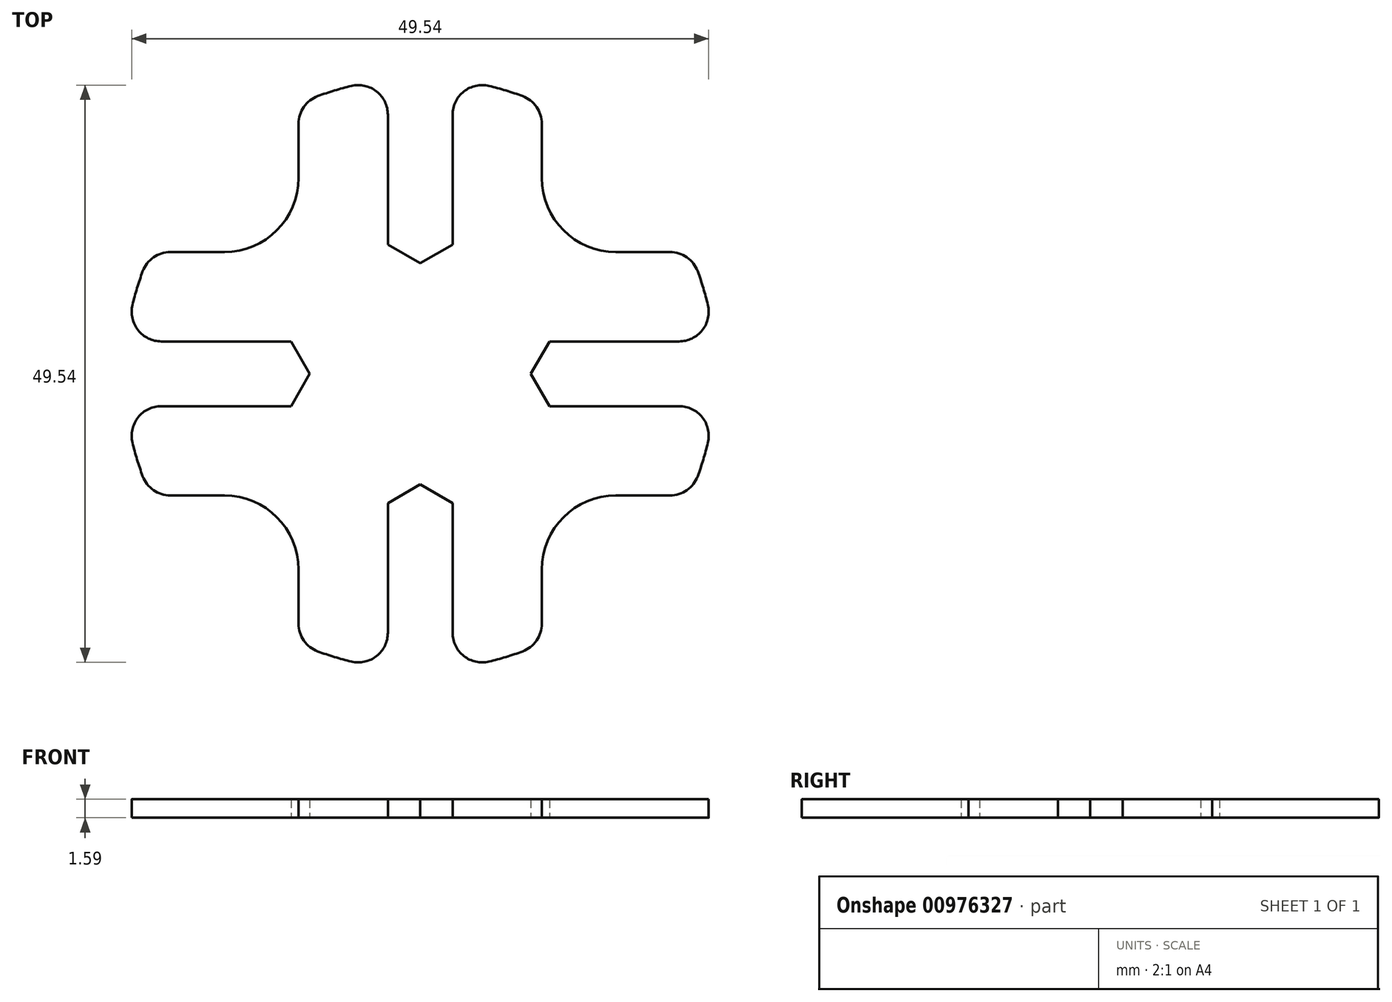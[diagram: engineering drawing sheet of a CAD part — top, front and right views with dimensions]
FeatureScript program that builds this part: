
annotation { "Feature Type Name" : "Feature", "Feature Type Description" : "" }
export const myFeature = defineFeature(function(context is Context, id is Id, definition is map)
    precondition{}
    {
        {
            var Q0;
            Q0=qCreatedBy(makeId("Top.planeOp"),FACE);
            var sketch = newSketch(context, id + "F0", { "sketchPlane" : qUnion([Q0])});
            skCircle(sketch, "E0", {"center": v(0, 0) * mm, "radius": 25.4 * mm});
            skCircle(sketch, "E1.cCircle", {"center": v(0, 12.7) * mm, "radius": 2.78 * mm, "construction": true});
            skLineSegment(sketch, "E1.0", {"start": v(-2.78, 11.1) * mm, "end": v(-2.78, 14.3) * mm});
            skLineSegment(sketch, "E1.1", {"start": v(-2.78, 14.3) * mm, "end": v(0, 15.9) * mm});
            skLineSegment(sketch, "E1.2", {"start": v(0, 15.9) * mm, "end": v(2.78, 14.3) * mm});
            skLineSegment(sketch, "E1.3", {"start": v(2.78, 14.3) * mm, "end": v(2.78, 11.1) * mm});
            skLineSegment(sketch, "E1.4", {"start": v(2.78, 11.1) * mm, "end": v(0, 9.5) * mm});
            skLineSegment(sketch, "E1.5", {"start": v(0, 9.5) * mm, "end": v(-2.78, 11.1) * mm});
            skPoint(sketch, "E1.0.midPoint", {"position": v(-2.78, 12.7) * mm});
            skLineSegment(sketch, "E2", {"start": v(-2.78, 14.3) * mm, "end": v(-2.78, 25.25) * mm});
            skLineSegment(sketch, "E3", {"start": v(2.78, 14.3) * mm, "end": v(2.78, 25.25) * mm});
            skCircle(sketch, "E4.cCircle", {"center": v(0, -12.7) * mm, "radius": 2.78 * mm, "construction": true});
            skLineSegment(sketch, "E4.0", {"start": v(-2.78, -11.1) * mm, "end": v(0, -9.5) * mm});
            skLineSegment(sketch, "E4.1", {"start": v(0, -9.5) * mm, "end": v(2.78, -11.1) * mm});
            skLineSegment(sketch, "E4.2", {"start": v(2.78, -11.1) * mm, "end": v(2.78, -14.3) * mm});
            skLineSegment(sketch, "E4.3", {"start": v(2.78, -14.3) * mm, "end": v(0, -15.9) * mm});
            skLineSegment(sketch, "E4.4", {"start": v(0, -15.9) * mm, "end": v(-2.78, -14.3) * mm});
            skLineSegment(sketch, "E4.5", {"start": v(-2.78, -14.3) * mm, "end": v(-2.78, -11.1) * mm});
            skPoint(sketch, "E4.0.midPoint", {"position": v(-1.39, -10.3) * mm});
            skCircle(sketch, "E5.cCircle", {"center": v(12.7, 0) * mm, "radius": 2.78 * mm, "construction": true});
            skLineSegment(sketch, "E5.0", {"start": v(9.5, 0) * mm, "end": v(11.1, 2.78) * mm});
            skLineSegment(sketch, "E5.1", {"start": v(11.1, 2.78) * mm, "end": v(14.3, 2.78) * mm});
            skLineSegment(sketch, "E5.2", {"start": v(14.3, 2.78) * mm, "end": v(15.9, 0) * mm});
            skLineSegment(sketch, "E5.3", {"start": v(15.9, 0) * mm, "end": v(14.3, -2.78) * mm});
            skLineSegment(sketch, "E5.4", {"start": v(14.3, -2.78) * mm, "end": v(11.1, -2.78) * mm});
            skLineSegment(sketch, "E5.5", {"start": v(11.1, -2.78) * mm, "end": v(9.5, 0) * mm});
            skPoint(sketch, "E5.0.midPoint", {"position": v(10.3, 1.39) * mm});
            skCircle(sketch, "E6.cCircle", {"center": v(-12.7, 0) * mm, "radius": 2.78 * mm, "construction": true});
            skLineSegment(sketch, "E6.0", {"start": v(-15.9, 0) * mm, "end": v(-14.3, 2.78) * mm});
            skLineSegment(sketch, "E6.1", {"start": v(-14.3, 2.78) * mm, "end": v(-11.1, 2.78) * mm});
            skLineSegment(sketch, "E6.2", {"start": v(-11.1, 2.78) * mm, "end": v(-9.5, 0) * mm});
            skLineSegment(sketch, "E6.3", {"start": v(-9.5, 0) * mm, "end": v(-11.1, -2.78) * mm});
            skLineSegment(sketch, "E6.4", {"start": v(-11.1, -2.78) * mm, "end": v(-14.3, -2.78) * mm});
            skLineSegment(sketch, "E6.5", {"start": v(-14.3, -2.78) * mm, "end": v(-15.9, 0) * mm});
            skPoint(sketch, "E6.0.midPoint", {"position": v(-15.1, 1.39) * mm});
            skLineSegment(sketch, "E7", {"start": v(-14.3, -2.78) * mm, "end": v(-25.25, -2.78) * mm});
            skLineSegment(sketch, "E8", {"start": v(-14.3, 2.78) * mm, "end": v(-25.25, 2.78) * mm});
            skLineSegment(sketch, "E9", {"start": v(14.3, 2.78) * mm, "end": v(25.25, 2.78) * mm});
            skLineSegment(sketch, "E10", {"start": v(14.3, -2.78) * mm, "end": v(25.25, -2.78) * mm});
            skLineSegment(sketch, "E11", {"start": v(2.78, -14.3) * mm, "end": v(2.78, -25.25) * mm});
            skLineSegment(sketch, "E12", {"start": v(-2.78, -14.3) * mm, "end": v(-2.78, -25.25) * mm});
            skLineSegment(sketch, "E13", {"start": v(-23.15, 10.45) * mm, "end": v(-10.45, 10.45) * mm});
            skLineSegment(sketch, "E14", {"start": v(-10.45, 10.45) * mm, "end": v(-10.45, 23.15) * mm});
            skLineSegment(sketch, "E15", {"start": v(-23.15, -10.45) * mm, "end": v(-10.45, -10.45) * mm});
            skLineSegment(sketch, "E16", {"start": v(-10.45, -10.45) * mm, "end": v(-10.45, -23.15) * mm});
            skLineSegment(sketch, "E17", {"start": v(10.45, -23.15) * mm, "end": v(10.45, -10.45) * mm});
            skLineSegment(sketch, "E18", {"start": v(10.45, -10.45) * mm, "end": v(23.15, -10.45) * mm});
            skLineSegment(sketch, "E19", {"start": v(23.15, 10.45) * mm, "end": v(10.45, 10.45) * mm});
            skLineSegment(sketch, "E20", {"start": v(10.45, 10.45) * mm, "end": v(10.45, 23.15) * mm});
            skSolve(sketch);
        }
        {
            var Q0;
            Q0=makeQuery(id+"F0.imprint","IMPRINT",FACE,{"disambiguationData":[TD([[makeQuery(id+"F0.imprint","IMPRINT",EDGE,{"derivedFrom":sQuery(id+"F0.wireOp",EDGE,"E1.0")}),1.0]])]});
            var Q1;
            {var subQ0=sQuery(id+"F0.wireOp",EDGE,"R65O2wjh-e6GP-hYqe-g3Ux-lFNkPaJh4EzS");Q1=makeQuery(id+"F0.imprint","IMPRINT",FACE,{"disambiguationData":[TD([[makeQuery(id+"F0.imprint","IMPRINT",EDGE,{"derivedFrom":subQ0}),-1.0]])]});}
            extrude(context, id + "F1", {"entities" : qUnion([Q0, Q1]), "depth" : 1.59 * mm, "offsetDistance" : 25.4 * mm});
        }
        {
            var Q0;
            Q0=makeQuery(id+"F1.opExtrude","SWEPT_EDGE",EDGE,{"disambiguationData":[OSD([sQuery(id+"F0.wireOp",EDGE,"E15"),sQuery(id+"F0.wireOp",EDGE,"E16")])]});
            var Q1;
            Q1=makeQuery(id+"F1.opExtrude","SWEPT_EDGE",EDGE,{"disambiguationData":[OSD([sQuery(id+"F0.wireOp",EDGE,"E17"),sQuery(id+"F0.wireOp",EDGE,"E18")])]});
            var Q2;
            Q2=makeQuery(id+"F1.opExtrude","SWEPT_EDGE",EDGE,{"disambiguationData":[OSD([sQuery(id+"F0.wireOp",EDGE,"E19"),sQuery(id+"F0.wireOp",EDGE,"E20")])]});
            var Q3;
            Q3=makeQuery(id+"F1.opExtrude","SWEPT_EDGE",EDGE,{"disambiguationData":[OSD([sQuery(id+"F0.wireOp",EDGE,"E13"),sQuery(id+"F0.wireOp",EDGE,"E14")])]});
            fillet(context, id + "F2", {"entities" : qUnion([Q0, Q1, Q2, Q3]), "radius" : 6.35 * mm, "tangentPropagation" : true, "allowEdgeOverflow" : false});
        }
        {
            var Q0;
            Q0=makeQuery(id+"F1.opExtrude","SWEPT_EDGE",EDGE,{"disambiguationData":[OSD([sQuery(id+"F0.wireOp",EDGE,"E0"),sQuery(id+"F0.wireOp",EDGE,"E3")])]});
            var Q1;
            Q1=makeQuery(id+"F1.opExtrude","SWEPT_EDGE",EDGE,{"disambiguationData":[OSD([sQuery(id+"F0.wireOp",EDGE,"E0"),sQuery(id+"F0.wireOp",EDGE,"E2")])]});
            var Q2;
            Q2=makeQuery(id+"F1.opExtrude","SWEPT_EDGE",EDGE,{"disambiguationData":[OSD([sQuery(id+"F0.wireOp",EDGE,"E0"),sQuery(id+"F0.wireOp",EDGE,"E9")])]});
            var Q3;
            Q3=makeQuery(id+"F1.opExtrude","SWEPT_EDGE",EDGE,{"disambiguationData":[OSD([sQuery(id+"F0.wireOp",EDGE,"E0"),sQuery(id+"F0.wireOp",EDGE,"E10")])]});
            var Q4;
            Q4=makeQuery(id+"F1.opExtrude","SWEPT_EDGE",EDGE,{"disambiguationData":[OSD([sQuery(id+"F0.wireOp",EDGE,"E0"),sQuery(id+"F0.wireOp",EDGE,"E11")])]});
            var Q5;
            Q5=makeQuery(id+"F1.opExtrude","SWEPT_EDGE",EDGE,{"disambiguationData":[OSD([sQuery(id+"F0.wireOp",EDGE,"E0"),sQuery(id+"F0.wireOp",EDGE,"E12")])]});
            var Q6;
            Q6=makeQuery(id+"F1.opExtrude","SWEPT_EDGE",EDGE,{"disambiguationData":[OSD([sQuery(id+"F0.wireOp",EDGE,"E0"),sQuery(id+"F0.wireOp",EDGE,"E7")])]});
            var Q7;
            Q7=makeQuery(id+"F1.opExtrude","SWEPT_EDGE",EDGE,{"disambiguationData":[OSD([sQuery(id+"F0.wireOp",EDGE,"E0"),sQuery(id+"F0.wireOp",EDGE,"E8")])]});
            var Q8;
            Q8=makeQuery(id+"F1.opExtrude","SWEPT_EDGE",EDGE,{"disambiguationData":[OSD([sQuery(id+"F0.wireOp",EDGE,"E0"),sQuery(id+"F0.wireOp",EDGE,"E19")])]});
            var Q9;
            Q9=makeQuery(id+"F1.opExtrude","SWEPT_EDGE",EDGE,{"disambiguationData":[OSD([sQuery(id+"F0.wireOp",EDGE,"E0"),sQuery(id+"F0.wireOp",EDGE,"E17")])]});
            var Q10;
            Q10=makeQuery(id+"F1.opExtrude","SWEPT_EDGE",EDGE,{"disambiguationData":[OSD([sQuery(id+"F0.wireOp",EDGE,"E0"),sQuery(id+"F0.wireOp",EDGE,"E16")])]});
            var Q11;
            Q11=makeQuery(id+"F1.opExtrude","SWEPT_EDGE",EDGE,{"disambiguationData":[OSD([sQuery(id+"F0.wireOp",EDGE,"E0"),sQuery(id+"F0.wireOp",EDGE,"E15")])]});
            var Q12;
            Q12=makeQuery(id+"F1.opExtrude","SWEPT_EDGE",EDGE,{"disambiguationData":[OSD([sQuery(id+"F0.wireOp",EDGE,"E0"),sQuery(id+"F0.wireOp",EDGE,"E13")])]});
            var Q13;
            Q13=makeQuery(id+"F1.opExtrude","SWEPT_EDGE",EDGE,{"disambiguationData":[OSD([sQuery(id+"F0.wireOp",EDGE,"E0"),sQuery(id+"F0.wireOp",EDGE,"E14")])]});
            var Q14;
            Q14=makeQuery(id+"F1.opExtrude","SWEPT_EDGE",EDGE,{"disambiguationData":[OSD([sQuery(id+"F0.wireOp",EDGE,"E0"),sQuery(id+"F0.wireOp",EDGE,"E20")])]});
            var Q15;
            Q15=makeQuery(id+"F1.opExtrude","SWEPT_EDGE",EDGE,{"disambiguationData":[OSD([sQuery(id+"F0.wireOp",EDGE,"E0"),sQuery(id+"F0.wireOp",EDGE,"E18")])]});
            fillet(context, id + "F3", {"entities" : qUnion([Q0, Q1, Q2, Q3, Q4, Q5, Q6, Q7, Q8, Q9, Q10, Q11, Q12, Q13, Q14, Q15]), "radius" : 2.54 * mm, "tangentPropagation" : true, "allowEdgeOverflow" : false});
        }
    });
